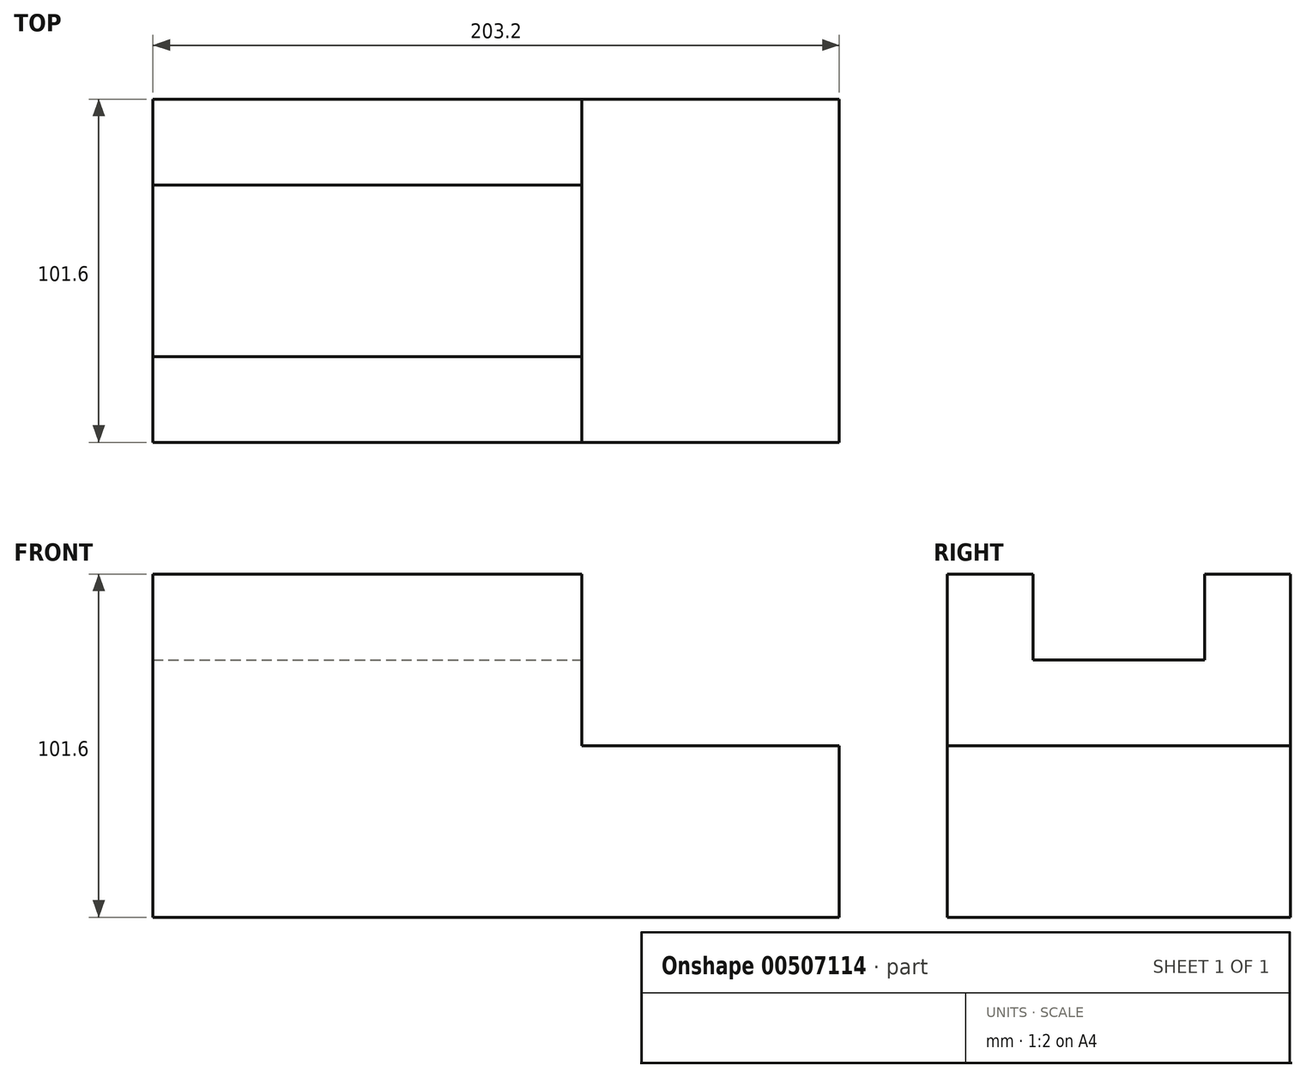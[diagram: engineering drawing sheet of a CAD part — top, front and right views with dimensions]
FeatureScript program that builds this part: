
annotation { "Feature Type Name" : "Feature", "Feature Type Description" : "" }
export const myFeature = defineFeature(function(context is Context, id is Id, definition is map)
    precondition{}
    {
        {
            var Q0;
            Q0=qCreatedBy(makeId("Top.planeOp"),FACE);
            var sketch = newSketch(context, id + "F0", { "sketchPlane" : qUnion([Q0])});
            skLineSegment(sketch, "E0.bottom", {"start": v(101.6, 50.8) * mm, "end": v(-101.6, 50.8) * mm});
            skLineSegment(sketch, "E0.top", {"start": v(101.6, -50.8) * mm, "end": v(-101.6, -50.8) * mm});
            skLineSegment(sketch, "E0.left", {"start": v(101.6, 50.8) * mm, "end": v(101.6, -50.8) * mm});
            skLineSegment(sketch, "E0.right", {"start": v(-101.6, 50.8) * mm, "end": v(-101.6, -50.8) * mm});
            skPoint(sketch, "E0.middle", {"position": v(0, 0) * mm});
            skSolve(sketch);
        }
        {
            var Q0;
            Q0 = qSketchRegion(id + "F0", true);
            extrude(context, id + "F1", {"entities" : qUnion([Q0]), "depth" : 101.6 * mm});
        }
        {
            var Q0;
            Q0=makeQuery(id+"F1.opExtrude","CAP_FACE",FACE,{"disambiguationData":[OSD([sQuery(id+"F0.wireOp",EDGE,"E0.bottom"),sQuery(id+"F0.wireOp",EDGE,"E0.top"),sQuery(id+"F0.wireOp",EDGE,"E0.left"),sQuery(id+"F0.wireOp",EDGE,"E0.right")])],"isStart":false});
            var sketch = newSketch(context, id + "F2", { "sketchPlane" : qUnion([Q0])});
            skLineSegment(sketch, "E1.bottom", {"start": v(101.6, 50.8) * mm, "end": v(25.4, 50.8) * mm});
            skLineSegment(sketch, "E1.top", {"start": v(101.6, -50.8) * mm, "end": v(25.4, -50.8) * mm});
            skLineSegment(sketch, "E1.left", {"start": v(101.6, 50.8) * mm, "end": v(101.6, -50.8) * mm});
            skLineSegment(sketch, "E1.right", {"start": v(25.4, 50.8) * mm, "end": v(25.4, -50.8) * mm});
            skSolve(sketch);
        }
        {
            var Q0;
            Q0 = qSketchRegion(id + "F2", true);
            var Q1;
            Q1=makeQuery(id+"F2.imprint","IMPRINT",FACE,{"disambiguationData":[TD([[makeQuery(id+"F2.imprint","IMPRINT",EDGE,{"derivedFrom":sQuery(id+"F2.wireOp",EDGE,"E1.bottom")}),1.0]])]});
            extrude(context, id + "F3", {"entities" : qUnion([Q0, Q1]), "operationType" : NewBodyOperationType.REMOVE, "oppositeDirection" : true, "depth" : 50.8 * mm});
        }
        {
            var Q0;
            Q0=makeQuery(id+"F1.opExtrude","CAP_FACE",FACE,{"disambiguationData":[OSD([sQuery(id+"F0.wireOp",EDGE,"E0.bottom"),sQuery(id+"F0.wireOp",EDGE,"E0.top"),sQuery(id+"F0.wireOp",EDGE,"E0.left"),sQuery(id+"F0.wireOp",EDGE,"E0.right")])],"isStart":false});
            var sketch = newSketch(context, id + "F4", { "sketchPlane" : qUnion([Q0])});
            skLineSegment(sketch, "E2.bottom", {"start": v(-101.6, 25.4) * mm, "end": v(25.4, 25.4) * mm});
            skLineSegment(sketch, "E2.top", {"start": v(-101.6, -25.4) * mm, "end": v(25.4, -25.4) * mm});
            skLineSegment(sketch, "E2.left", {"start": v(-101.6, 25.4) * mm, "end": v(-101.6, -25.4) * mm});
            skLineSegment(sketch, "E2.right", {"start": v(25.4, 25.4) * mm, "end": v(25.4, -25.4) * mm});
            skSolve(sketch);
        }
        {
            var Q0;
            Q0 = qSketchRegion(id + "F4", true);
            var Q1;
            Q1=makeQuery(id+"F4.imprint","IMPRINT",FACE,{"disambiguationData":[TD([[makeQuery(id+"F4.imprint","IMPRINT",EDGE,{"derivedFrom":sQuery(id+"F4.wireOp",EDGE,"E2.bottom")}),-1.0]])]});
            extrude(context, id + "F5", {"entities" : qUnion([Q0, Q1]), "operationType" : NewBodyOperationType.REMOVE, "oppositeDirection" : true, "depth" : 25.4 * mm});
        }
    });
